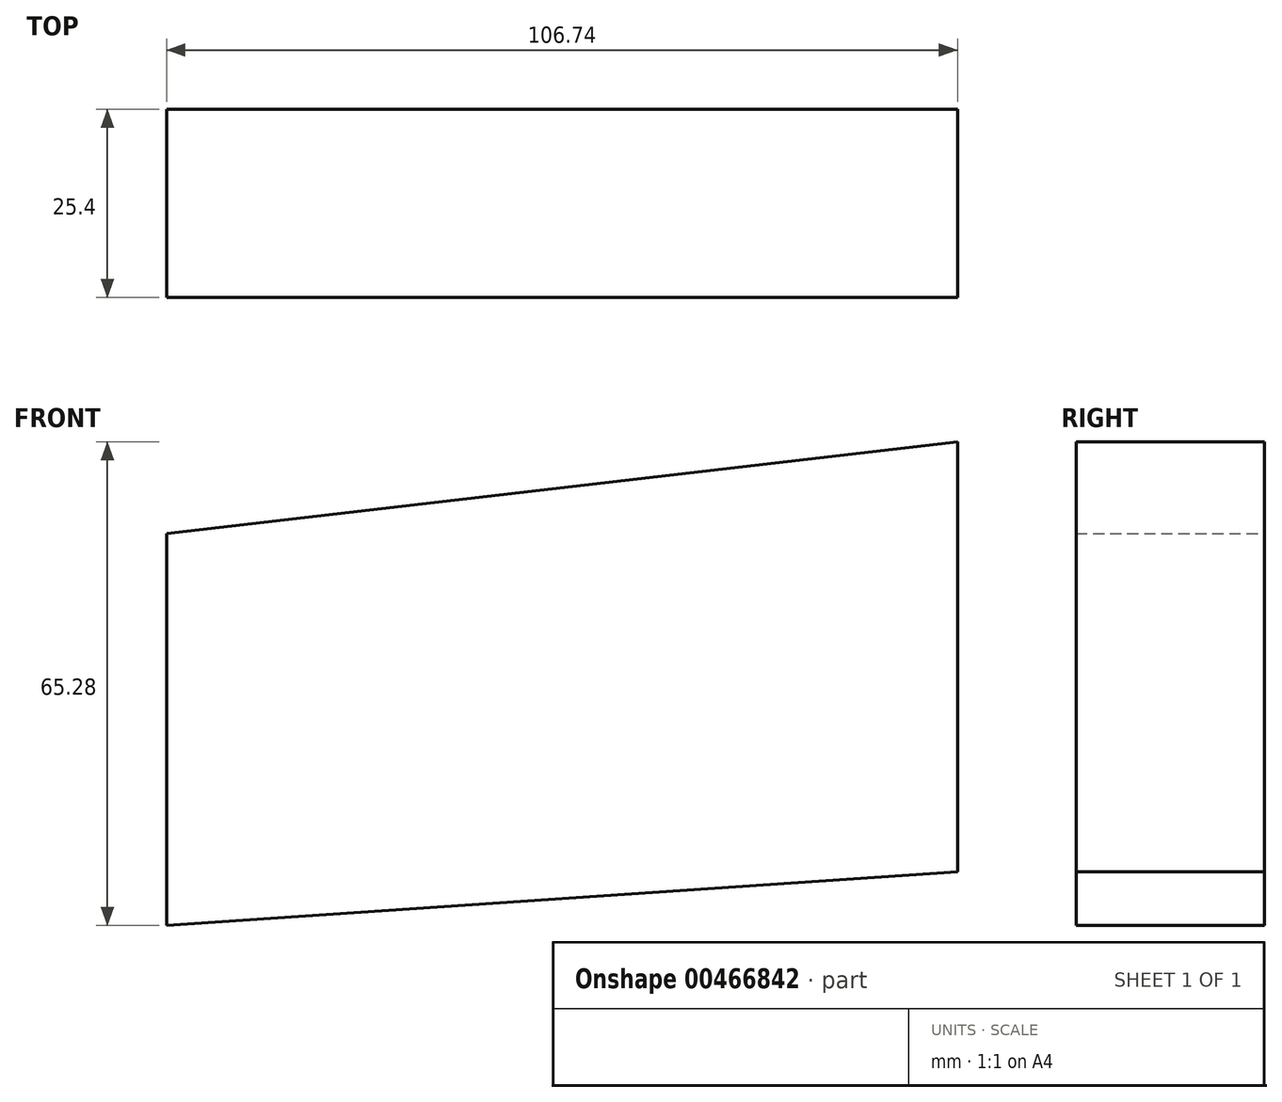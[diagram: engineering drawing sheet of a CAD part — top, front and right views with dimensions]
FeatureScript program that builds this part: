
annotation { "Feature Type Name" : "Feature", "Feature Type Description" : "" }
export const myFeature = defineFeature(function(context is Context, id is Id, definition is map)
    precondition{}
    {
        {
            var Q0;
            Q0=qCreatedBy(makeId("Front.planeOp"),FACE);
            var sketch = newSketch(context, id + "F0", { "sketchPlane" : qUnion([Q0])});
            skLineSegment(sketch, "E0", {"start": v(-79.15, 0) * mm, "end": v(-79.15, -52.92) * mm});
            skLineSegment(sketch, "E1", {"start": v(-79.15, -52.92) * mm, "end": v(27.59, -45.65) * mm});
            skLineSegment(sketch, "E2", {"start": v(27.59, -45.65) * mm, "end": v(27.59, 12.36) * mm});
            skLineSegment(sketch, "E3", {"start": v(27.59, 12.36) * mm, "end": v(-79.15, 0) * mm});
            skLineSegment(sketch, "E4", {"start": v(127.03, -20.18) * mm, "end": v(139.16, 29.32) * mm});
            skSolve(sketch);
        }
        {
            var Q0;
            Q0=makeQuery(id+"F0.imprint","IMPRINT",FACE,{"disambiguationData":[TD([[makeQuery(id+"F0.imprint","IMPRINT",EDGE,{"derivedFrom":sQuery(id+"F0.wireOp",EDGE,"E0")}),1.0]])]});
            extrude(context, id + "F1", {"entities" : qUnion([Q0]), "depth" : 25.4 * mm});
        }
    });
